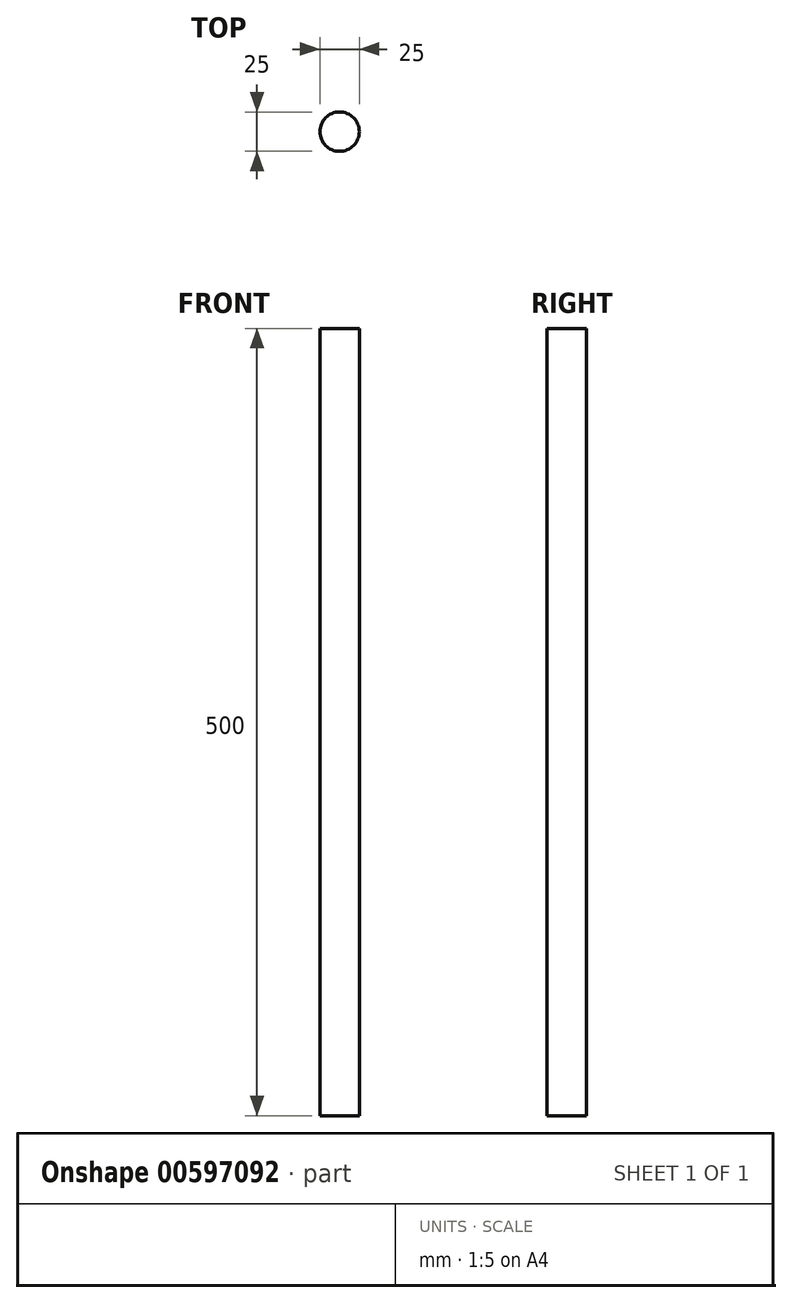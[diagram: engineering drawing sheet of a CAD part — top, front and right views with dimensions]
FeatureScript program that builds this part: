
annotation { "Feature Type Name" : "Feature", "Feature Type Description" : "" }
export const myFeature = defineFeature(function(context is Context, id is Id, definition is map)
    precondition{}
    {
        {
            var Q0;
            Q0=qCreatedBy(makeId("Top.planeOp"),FACE);
            var sketch = newSketch(context, id + "F0", { "sketchPlane" : qUnion([Q0])});
            skCircle(sketch, "E0", {"center": v(0, 0) * mm, "radius": 12.5 * mm});
            skSolve(sketch);
        }
        {
            var Q0;
            Q0=makeQuery(id+"F0.imprint","IMPRINT",FACE,{"disambiguationData":[TD([[makeQuery(id+"F0.imprint","IMPRINT",EDGE,{"derivedFrom":sQuery(id+"F0.wireOp",EDGE,"E0")}),1.0]])]});
            extrude(context, id + "F1", {"entities" : qUnion([Q0]), "depth" : 500 * mm, "offsetDistance" : 25.4 * mm});
        }
    });
